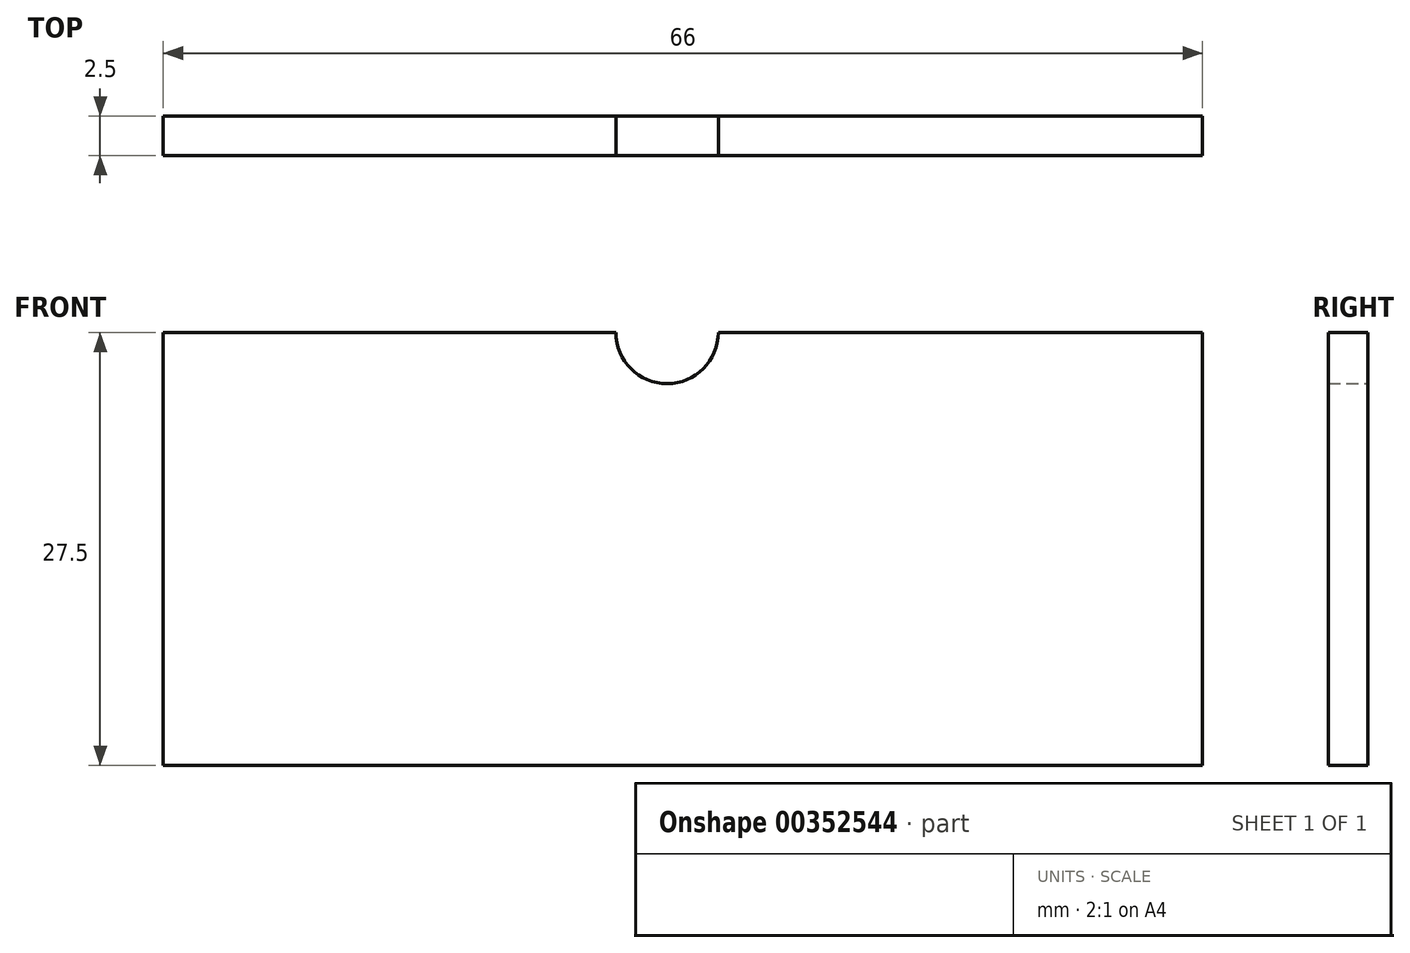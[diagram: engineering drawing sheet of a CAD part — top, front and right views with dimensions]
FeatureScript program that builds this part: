
annotation { "Feature Type Name" : "Feature", "Feature Type Description" : "" }
export const myFeature = defineFeature(function(context is Context, id is Id, definition is map)
    precondition{}
    {
        {
            var Q0;
            Q0=qCreatedBy(makeId("Front.planeOp"),FACE);
            var sketch = newSketch(context, id + "F0", { "sketchPlane" : qUnion([Q0])});
            skLineSegment(sketch, "E0.bottom", {"start": v(-33, 0) * mm, "end": v(33, 0) * mm});
            skLineSegment(sketch, "E0.top", {"start": v(-33, 27.5) * mm, "end": v(-4.25, 27.5) * mm});
            skLineSegment(sketch, "E0.left", {"start": v(-33, 0) * mm, "end": v(-33, 27.5) * mm});
            skLineSegment(sketch, "E0.right", {"start": v(33, 0) * mm, "end": v(33, 27.5) * mm});
            skArc(sketch, "E1", {"start": v(-4.25, 27.5) * mm, "mid": v(-1, 24.25) * mm, "end": v(2.25, 27.5) * mm});
            skLineSegment(sketch, "E2.trimOffspring", {"start": v(2.25, 27.5) * mm, "end": v(33, 27.5) * mm});
            skPoint(sketch, "E3", {"position": v(0, 0) * mm});
            skSolve(sketch);
        }
        {
            var Q0;
            Q0 = qSketchRegion(id + "F0", true);
            extrude(context, id + "F1", {"entities" : qUnion([Q0]), "depth" : 2.5 * mm});
        }
    });
